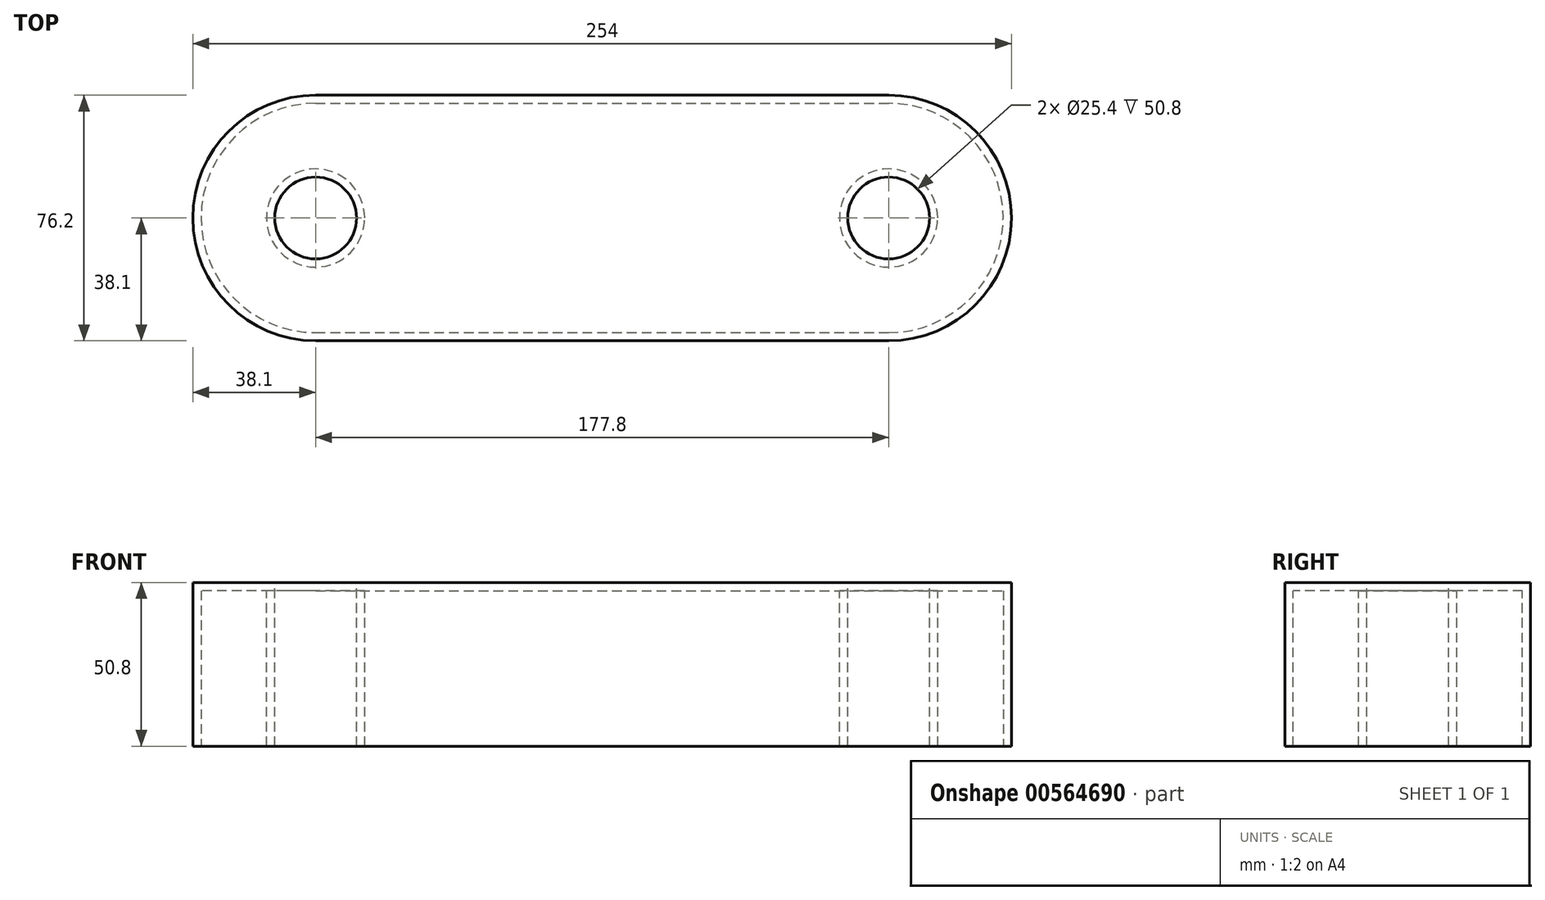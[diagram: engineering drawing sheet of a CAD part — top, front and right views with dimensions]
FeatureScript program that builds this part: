
annotation { "Feature Type Name" : "Feature", "Feature Type Description" : "" }
export const myFeature = defineFeature(function(context is Context, id is Id, definition is map)
    precondition{}
    {
        {
            var Q0;
            Q0=qCreatedBy(makeId("Top.planeOp"),FACE);
            var sketch = newSketch(context, id + "F0", { "sketchPlane" : qUnion([Q0])});
            skLineSegment(sketch, "E0.bottom", {"start": v(-88.9, 38.1) * mm, "end": v(88.9, 38.1) * mm});
            skLineSegment(sketch, "E0.top", {"start": v(-88.9, -38.1) * mm, "end": v(88.9, -38.1) * mm});
            skLineSegment(sketch, "E0.left", {"start": v(-127, 0) * mm, "end": v(-127, 0) * mm});
            skLineSegment(sketch, "E0.right", {"start": v(127, 0) * mm, "end": v(127, 0) * mm});
            skPoint(sketch, "E1.visualSharp", {"position": v(-127, 38.1) * mm});
            skArc(sketch, "E1.filletArc", {"start": v(-88.9, 38.1) * mm, "mid": v(-115.84, 26.94) * mm, "end": v(-127, 0) * mm});
            skPoint(sketch, "E2.visualSharp", {"position": v(-127, -38.1) * mm});
            skArc(sketch, "E2.filletArc", {"start": v(-127, 0) * mm, "mid": v(-115.84, -26.94) * mm, "end": v(-88.9, -38.1) * mm});
            skPoint(sketch, "E3.visualSharp", {"position": v(127, 38.1) * mm});
            skArc(sketch, "E3.filletArc", {"start": v(127, 0) * mm, "mid": v(115.84, 26.94) * mm, "end": v(88.9, 38.1) * mm});
            skPoint(sketch, "E4.visualSharp", {"position": v(127, -38.1) * mm});
            skArc(sketch, "E4.filletArc", {"start": v(88.9, -38.1) * mm, "mid": v(115.84, -26.94) * mm, "end": v(127, 0) * mm});
            skSolve(sketch);
        }
        {
            var Q0;
            Q0=makeQuery(id+"F0.imprint","IMPRINT",FACE,{"disambiguationData":[TD([[makeQuery(id+"F0.imprint","IMPRINT",EDGE,{"derivedFrom":sQuery(id+"F0.wireOp",EDGE,"E0.bottom")}),-1.0]])]});
            extrude(context, id + "F1", {"entities" : qUnion([Q0]), "depth" : 50.8 * mm, "offsetDistance" : 25.4 * mm});
        }
        {
            var Q0;
            Q0=makeQuery(id+"F1.opExtrude","CAP_FACE",FACE,{"disambiguationData":[OSD([sQuery(id+"F0.wireOp",EDGE,"E0.bottom"),sQuery(id+"F0.wireOp",EDGE,"E0.top"),sQuery(id+"F0.wireOp",EDGE,"E1.filletArc"),sQuery(id+"F0.wireOp",EDGE,"E2.filletArc"),sQuery(id+"F0.wireOp",EDGE,"E3.filletArc"),sQuery(id+"F0.wireOp",EDGE,"E4.filletArc")])],"isStart":false});
            var sketch = newSketch(context, id + "F2", { "sketchPlane" : qUnion([Q0])});
            skPoint(sketch, "E5", {"position": v(-88.9, 0) * mm});
            skPoint(sketch, "E6", {"position": v(88.9, 0) * mm});
            skSolve(sketch);
        }
        {
            var Q0;
            Q0=sQuery(id+"F2.wireOp",VERTEX,"E5");
            var Q1;
            Q1=sQuery(id+"F2.wireOp",VERTEX,"E6");
            var Q2;
            Q2=makeQuery(id+"F1.opExtrude","SWEPT_BODY",BODY,{"disambiguationData":[OSD([sQuery(id+"F0.wireOp",EDGE,"E0.bottom"),sQuery(id+"F0.wireOp",EDGE,"E0.top"),sQuery(id+"F0.wireOp",EDGE,"E1.filletArc"),sQuery(id+"F0.wireOp",EDGE,"E2.filletArc"),sQuery(id+"F0.wireOp",EDGE,"E3.filletArc"),sQuery(id+"F0.wireOp",EDGE,"E4.filletArc")])]});
            hole(context, id + "F3", {"style" : HoleStyle.SIMPLE, "endStyle" : HoleEndStyle.THROUGH, "holeDiameter" : 25.4 * mm, "isTappedThrough" : true, "tappedDepth" : 12.7 * mm, "tapClearance" : 3, "locations" : qUnion([Q0, Q1]), "scope" : qUnion([Q2])});
        }
        {
            var Q0;
            Q0=makeQuery(id+"F1.opExtrude","CAP_FACE",FACE,{"disambiguationData":[OSD([sQuery(id+"F0.wireOp",EDGE,"E0.bottom"),sQuery(id+"F0.wireOp",EDGE,"E0.top"),sQuery(id+"F0.wireOp",EDGE,"E1.filletArc"),sQuery(id+"F0.wireOp",EDGE,"E2.filletArc"),sQuery(id+"F0.wireOp",EDGE,"E3.filletArc"),sQuery(id+"F0.wireOp",EDGE,"E4.filletArc")])],"isStart":true});
            shell(context, id + "F4", {"entities" : qUnion([Q0]), "thickness" : 2.54 * mm});
        }
    });
